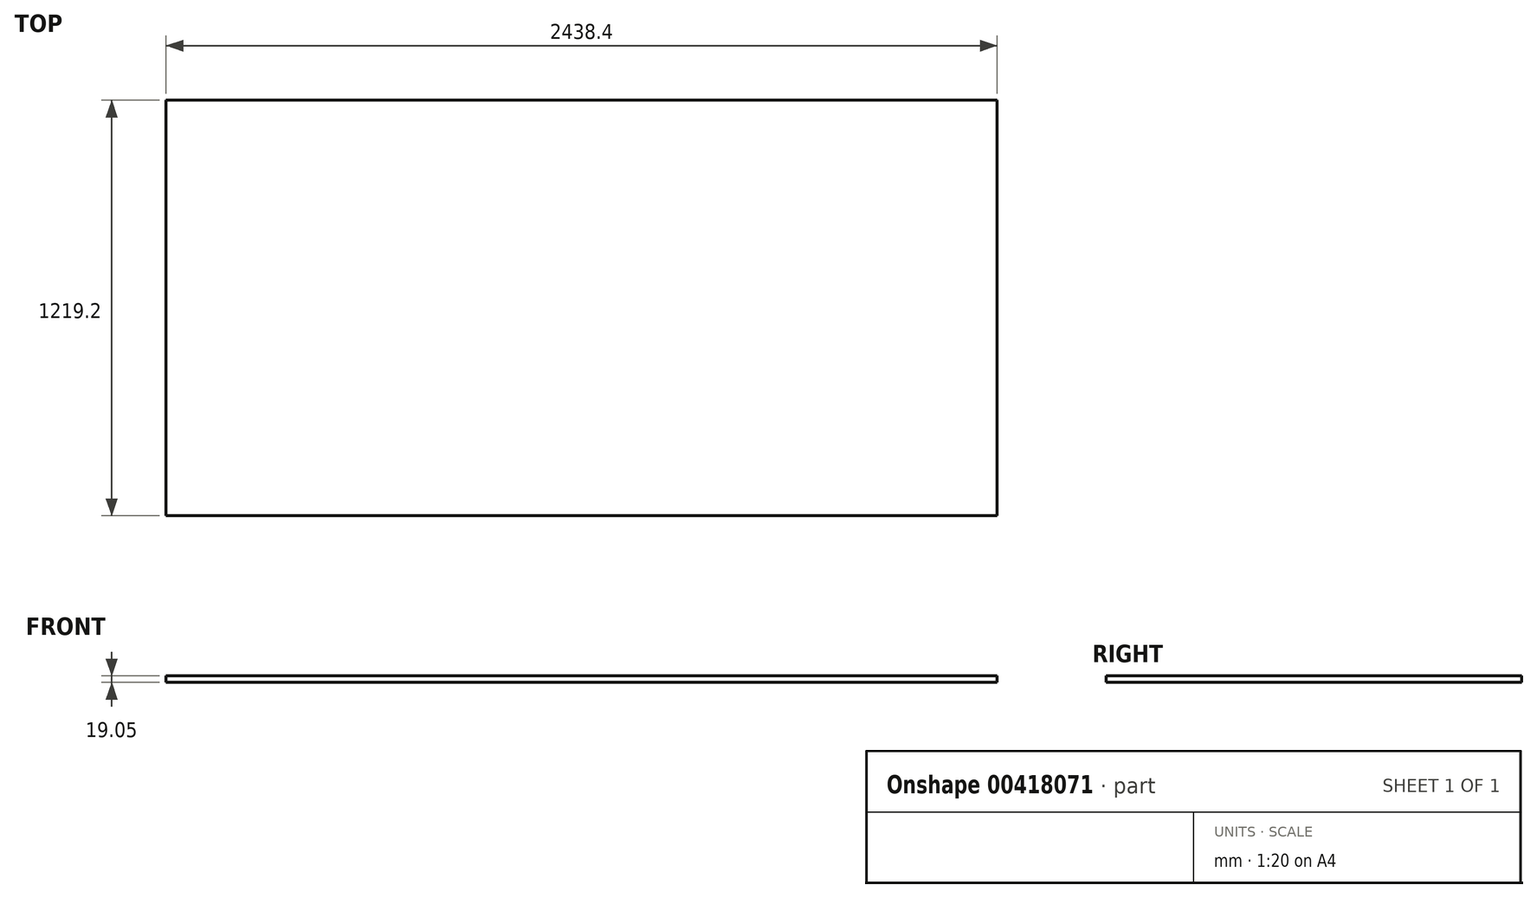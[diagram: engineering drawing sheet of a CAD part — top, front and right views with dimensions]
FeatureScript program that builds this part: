
annotation { "Feature Type Name" : "Feature", "Feature Type Description" : "" }
export const myFeature = defineFeature(function(context is Context, id is Id, definition is map)
    precondition{}
    {
        {
            var Q0;
            Q0=qCreatedBy(makeId("Top.planeOp"),FACE);
            var sketch = newSketch(context, id + "F0", { "sketchPlane" : qUnion([Q0])});
            skLineSegment(sketch, "E0.bottom", {"start": v(1219.2, -609.6) * mm, "end": v(-1219.2, -609.6) * mm});
            skLineSegment(sketch, "E0.top", {"start": v(1219.2, 609.6) * mm, "end": v(-1219.2, 609.6) * mm});
            skLineSegment(sketch, "E0.left", {"start": v(1219.2, -609.6) * mm, "end": v(1219.2, 609.6) * mm});
            skLineSegment(sketch, "E0.right", {"start": v(-1219.2, -609.6) * mm, "end": v(-1219.2, 609.6) * mm});
            skPoint(sketch, "E0.middle", {"position": v(0, 0) * mm});
            skSolve(sketch);
        }
        {
            var Q0;
            Q0=makeQuery(id+"F0.imprint","IMPRINT",FACE,{"disambiguationData":[TD([[makeQuery(id+"F0.imprint","IMPRINT",EDGE,{"derivedFrom":sQuery(id+"F0.wireOp",EDGE,"E0.bottom")}),-1.0]])]});
            extrude(context, id + "F1", {"entities" : qUnion([Q0]), "depth" : 19.05 * mm});
        }
    });
